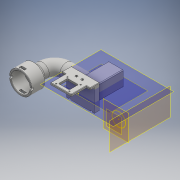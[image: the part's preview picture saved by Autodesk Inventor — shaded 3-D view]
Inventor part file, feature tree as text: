
AUTODESK INVENTOR PART (.ipt)
format: ipt  version: 2016 (Build 200138000, 138)  size: 643,584 bytes
history: native  units: mm
features: sketch x28, extrude x24, fillet x10, other x8, projected_geometry x3, loft x2, sweep x1, mirror x1
ambient origin geometry x8: Origin, YZ Plane, XZ Plane, XY Plane, X Axis, Y Axis, Z Axis, Center Point
bodies: Body1 (feature_tree)
feature tree (77):
  other  "ソリッド1"
  extrude  "押し出し1"  Depth=13.0mm TaperAngle=0.0deg
  fillet  "フィレット1"  Radius=1.0mm
  fillet  "フィレット2"  Radius=10.0mm
  sketch  "スケッチ2"
  extrude  "押し出し2"  Depth=10.0mm
  extrude  "押し出し3"  Depth=4.0mm TaperAngle=0.0deg
  sketch  "スケッチ3"
  extrude  "押し出し4"  Depth=4.0mm TaperAngle=0.0deg
  extrude  "押し出し5"  Depth=13.0mm
  extrude  "押し出し6"  Depth=13.0mm
  extrude  "押し出し7"  Depth=7.0mm TaperAngle=0.0deg
  fillet  "フィレット3"  Radius=7.0mm
  extrude  "押し出し8"  Depth=40.0mm
  extrude  "押し出し9"  Depth=40.0mm
  sketch  "スケッチ9"
  other  "作業平面1"
  sweep  "スイープ1"
  extrude  "押し出し10"  Depth=17.5mm
  sketch  "スケッチ12"
  other  "作業平面2"
  loft  "ロフト1"
  other  "作業平面3"
  loft  "ロフト2"
  extrude  "押し出し11"  Depth=25.0mm
  extrude  "押し出し12"  Depth=55.0mm TaperAngle=0.0deg
  fillet  "フィレット4"  Radius=20.0mm
  fillet  "フィレット5"  Radius=2.0mm
  other  "作業平面4"
  extrude  "押し出し13"  Depth=4.0mm
  other  "作業平面5"
  extrude  "押し出し14"  Depth=4.0mm
  extrude  "押し出し15"  Depth=4.0mm
  fillet  "フィレット6"  Radius=4.0mm
  fillet  "フィレット7"  Radius=2.0mm
  extrude  "押し出し20"  Depth=90.0mm TaperAngle=0.0deg
  extrude  "押し出し21"  Depth=4.0mm
  fillet  "フィレット8"  Radius=73.0mm
  fillet  "フィレット9"  Radius=14.0mm
  extrude  "押し出し22"  TaperAngle=90.0deg  [1 undecoded]
  extrude  "押し出し23"  TaperAngle=0.0deg  [1 undecoded]
  extrude  "押し出し24"  Depth=12.0mm TaperAngle=0.0deg
  extrude  "押し出し25"  Depth=12.0mm
  extrude  "押し出し26"  Depth=60.0mm
  extrude  "押し出し27"  TaperAngle=0.0deg  [1 undecoded]
  extrude  "押し出し28"  TaperAngle=0.0deg  [1 undecoded]
  fillet  "フィレット10"  [1 undecoded]
  mirror  "ミラー1"
  sketch  "スケッチ1"
  sketch  "スケッチ4"
  sketch  "スケッチ5"
  sketch  "スケッチ6"
  sketch  "スケッチ7"
  sketch  "スケッチ10"
  sketch  "スケッチ11"
  projected_geometry  "投影ループ1"
  sketch  "スケッチ13"
  other  "エッジ1"
  sketch  "スケッチ15"
  sketch  "スケッチ18"
  sketch  "スケッチ19"
  sketch  "スケッチ20"
  projected_geometry  "投影ループ2"
  sketch  "スケッチ21"
  sketch  "スケッチ22"
  sketch  "スケッチ23"
  sketch  "スケッチ27"
  sketch  "スケッチ28"
  sketch  "スケッチ29"
  projected_geometry  "投影ループ3"
  sketch  "スケッチ30"
  sketch  "スケッチ31"
  sketch  "スケッチ32"
  sketch  "スケッチ33"
  sketch  "スケッチ34"
  sketch  "スケッチ35"
  other  "断面エッジを投影1"
note: 5 required parameter values undecoded (feature->parameter linkage not recoverable at this tier; creation-order binding heuristic only, values carry confidence <= 0.55)
